# Revit family: EKF_EE_МонтажнаяПлатаДляУстановкиВыкатногоИСтационарногоВАTrivia_AVERES
name_source: partatom
category: Электрооборудование
units: mm (PartAtom-declared; Revit-internal decimal feet)

## family parameters
Всегда вертикально = Нет
На основе рабочей плоскости = Да
Общий = Да
При загрузке вырезать с полостями = Нет
Размер круглого соединителя = Использовать диаметр
Тип детали = Силовой щит
Точка расчета площади = Нет

## types (6) — shared parameters
ADSK_Единица измерения = шт.
ADSK_Завод-изготовитель = EKF
ADSK_Количество = 1
ADSK_Материал = RAL 7035_Сталь
ADSK_Размер_Глубина = 20 мм
Изготовитель = EKF
Отметка по умолчанию = 1219.2 мм
Серия номенклатуры = Averes
Степень защиты IP = -
ТВ = EKF_2_TRIVIA_AVERES
Тип установки = -
Тип_Платы = Монтажная плата 2
zero-valued in all types: ADSK_Масса

## per-type parameters (varying)
| type | ADSK_Код изделия | ADSK_Размер_Высота | ADSK_Размер_Ширина | Тип |
| Монтажная плата для установки ВА-450 3Р/4Р стац./выкатн. EKF AVERES | MPFU4701 | 282 мм | 564 мм | 553 мм |
| Монтажная плата для установки выкатного ВА-45/2000 3Р/4Р EKF AVERES | MPFU4401 | 322 мм | 564 мм | 554 мм |
| Монтажная плата для установки выкатного ВА-45/3200 3Р/4Р EKF AVERES | MPFU4501 | 322 мм | 564 мм | 555 мм |
| Монтажная плата для установки выкатного ВА-45/4000 3Р/4Р EKF AVERES | MPFU4601 | 337 мм | 764 мм | 556 мм |
| Монтажная плата для установки стационарного ВА-45/2000 3Р/4Р EKF AVERES | MPFU4201 | 302 мм | 564 мм | 557 мм |
| Монтажная плата для установки стационарного ВА-45/3200 3Р/4Р EKF AVERES | MPFU4301 | 302 мм | 564 мм | 558 мм |

note: column(s) folded — value = type name in every type: ADSK_Марка, ADSK_Наименование, ADSK_Обозначение
